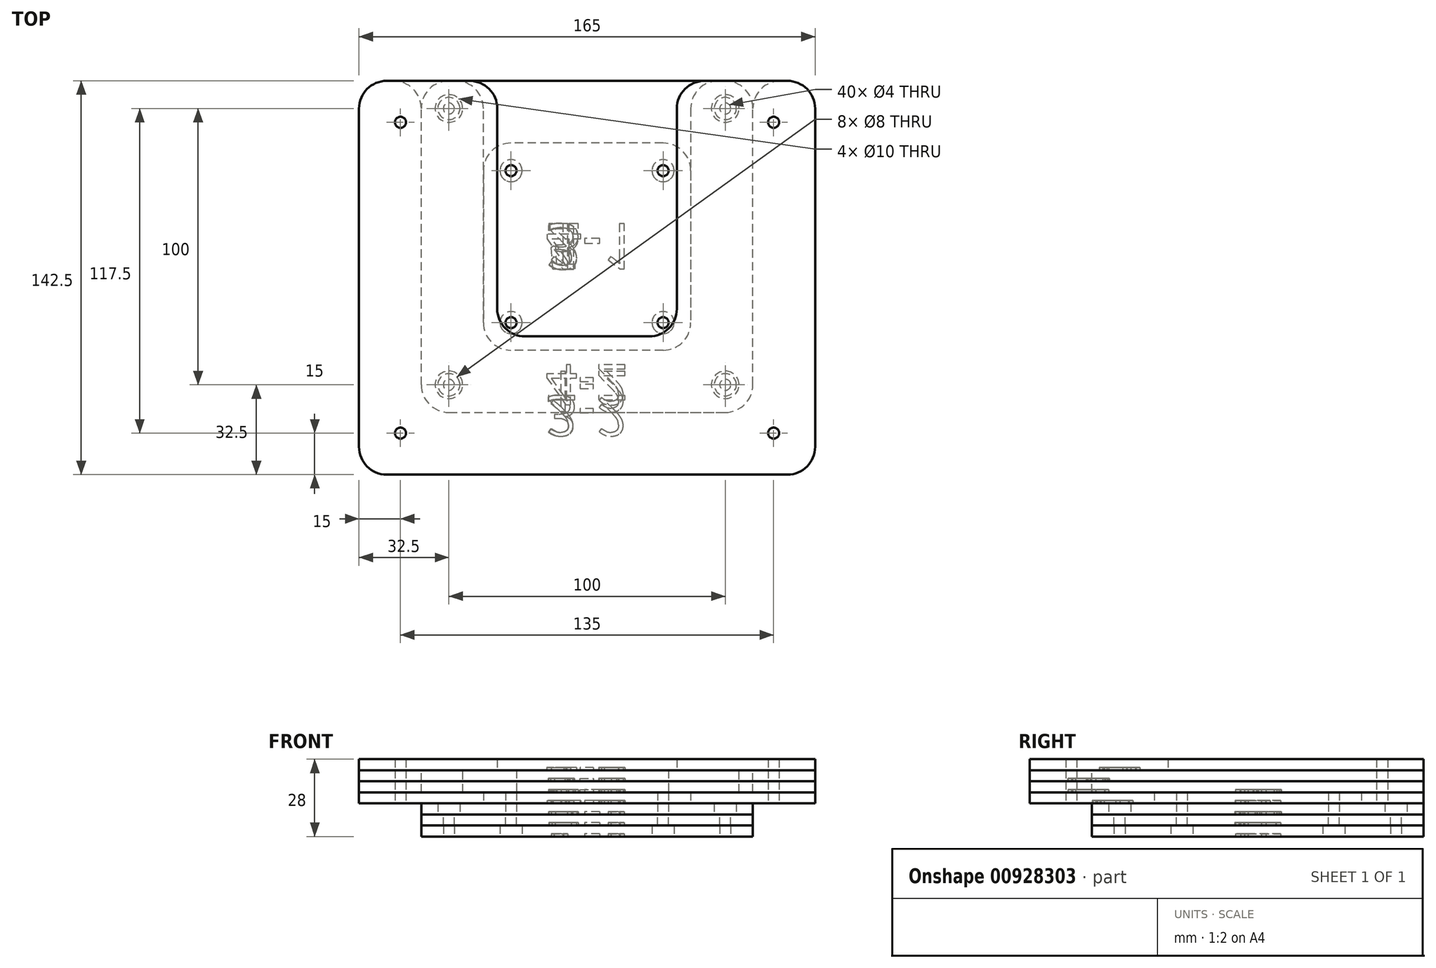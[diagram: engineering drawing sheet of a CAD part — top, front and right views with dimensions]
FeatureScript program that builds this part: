
annotation { "Feature Type Name" : "Feature", "Feature Type Description" : "" }
export const myFeature = defineFeature(function(context is Context, id is Id, definition is map)
    precondition{}
    {
        {
            var Q0;
            Q0=qCreatedBy(makeId("Top.planeOp"),FACE);
            var sketch = newSketch(context, id + "F0", { "sketchPlane" : qUnion([Q0])});
            skLineSegment(sketch, "E0.bottom", {"start": v(50, 50) * mm, "end": v(-50, 50) * mm, "construction": true});
            skLineSegment(sketch, "E0.top", {"start": v(50, -50) * mm, "end": v(-50, -50) * mm, "construction": true});
            skLineSegment(sketch, "E0.left", {"start": v(50, 50) * mm, "end": v(50, -50) * mm, "construction": true});
            skLineSegment(sketch, "E0.right", {"start": v(-50, 50) * mm, "end": v(-50, -50) * mm, "construction": true});
            skPoint(sketch, "E0.middle", {"position": v(0, 0) * mm});
            skCircle(sketch, "E1", {"center": v(-50, 50) * mm, "radius": 2 * mm});
            skCircle(sketch, "E2", {"center": v(50, 50) * mm, "radius": 2 * mm});
            skCircle(sketch, "E3", {"center": v(50, -50) * mm, "radius": 2 * mm});
            skCircle(sketch, "E4", {"center": v(-50, -50) * mm, "radius": 2 * mm});
            skLineSegment(sketch, "E5.bottom", {"start": v(60, 60) * mm, "end": v(-60, 60) * mm});
            skLineSegment(sketch, "E5.top", {"start": v(60, -60) * mm, "end": v(-60, -60) * mm});
            skLineSegment(sketch, "E5.left", {"start": v(60, 60) * mm, "end": v(60, -60) * mm});
            skLineSegment(sketch, "E5.right", {"start": v(-60, 60) * mm, "end": v(-60, -60) * mm});
            skSolve(sketch);
        }
        {
            var Q0;
            Q0 = qSketchRegion(id + "F0", true);
            extrude(context, id + "F1", {"entities" : qUnion([Q0]), "depth" : 4 * mm, "offsetDistance" : 25 * mm});
        }
        {
            var Q0;
            Q0=makeQuery(id+"F1.opExtrude","SWEPT_EDGE",EDGE,{"disambiguationData":[OSD([sQuery(id+"F0.wireOp",EDGE,"E5.bottom"),sQuery(id+"F0.wireOp",EDGE,"E5.right")])]});
            var Q1;
            Q1=makeQuery(id+"F1.opExtrude","SWEPT_EDGE",EDGE,{"disambiguationData":[OSD([sQuery(id+"F0.wireOp",EDGE,"E5.bottom"),sQuery(id+"F0.wireOp",EDGE,"E5.left")])]});
            var Q2;
            Q2=makeQuery(id+"F1.opExtrude","SWEPT_EDGE",EDGE,{"disambiguationData":[OSD([sQuery(id+"F0.wireOp",EDGE,"E5.top"),sQuery(id+"F0.wireOp",EDGE,"E5.right")])]});
            var Q3;
            Q3=makeQuery(id+"F1.opExtrude","SWEPT_EDGE",EDGE,{"disambiguationData":[OSD([sQuery(id+"F0.wireOp",EDGE,"E5.top"),sQuery(id+"F0.wireOp",EDGE,"E5.left")])]});
            fillet(context, id + "F2", {"entities" : qUnion([Q0, Q1, Q2, Q3]), "radius" : 10 * mm, "tangentPropagation" : true, "allowEdgeOverflow" : false});
        }
        {
            var Q0;
            Q0=makeQuery(id+"F1.opExtrude","CAP_FACE",FACE,{"disambiguationData":[OSD([sQuery(id+"F0.wireOp",EDGE,"E1"),sQuery(id+"F0.wireOp",EDGE,"E2"),sQuery(id+"F0.wireOp",EDGE,"E3"),sQuery(id+"F0.wireOp",EDGE,"E4"),sQuery(id+"F0.wireOp",EDGE,"E5.bottom"),sQuery(id+"F0.wireOp",EDGE,"E5.top"),sQuery(id+"F0.wireOp",EDGE,"E5.left"),sQuery(id+"F0.wireOp",EDGE,"E5.right")])],"isStart":false});
            var sketch = newSketch(context, id + "F3", { "sketchPlane" : qUnion([Q0])});
            skLineSegment(sketch, "E6.0.0", {"start": v(-50, -60) * mm, "end": v(50, -60) * mm});
            skArc(sketch, "E6.0.1", {"start": v(50, -60) * mm, "mid": v(57.07, -57.07) * mm, "end": v(60, -50) * mm});
            skLineSegment(sketch, "E6.0.2", {"start": v(60, -50) * mm, "end": v(60, 50) * mm});
            skArc(sketch, "E6.0.3", {"start": v(60, 50) * mm, "mid": v(57.07, 57.07) * mm, "end": v(50, 60) * mm});
            skLineSegment(sketch, "E6.0.4", {"start": v(50, 60) * mm, "end": v(-50, 60) * mm});
            skArc(sketch, "E6.0.5", {"start": v(-50, 60) * mm, "mid": v(-57.07, 57.07) * mm, "end": v(-60, 50) * mm});
            skLineSegment(sketch, "E6.0.6", {"start": v(-60, 50) * mm, "end": v(-60, -50) * mm});
            skArc(sketch, "E6.0.7", {"start": v(-60, -50) * mm, "mid": v(-57.07, -57.07) * mm, "end": v(-50, -60) * mm});
            skCircle(sketch, "E7.0", {"center": v(-50, 50) * mm, "radius": 2 * mm, "construction": true});
            skCircle(sketch, "E8.0", {"center": v(50, 50) * mm, "radius": 2 * mm, "construction": true});
            skCircle(sketch, "E9.0", {"center": v(50, -50) * mm, "radius": 2 * mm, "construction": true});
            skCircle(sketch, "E10.0", {"center": v(-50, -50) * mm, "radius": 2 * mm, "construction": true});
            skCircle(sketch, "E11", {"center": v(-50, 50) * mm, "radius": 4 * mm});
            skCircle(sketch, "E12", {"center": v(50, 50) * mm, "radius": 4 * mm});
            skCircle(sketch, "E13", {"center": v(50, -50) * mm, "radius": 4 * mm});
            skCircle(sketch, "E14", {"center": v(-50, -50) * mm, "radius": 4 * mm});
            skSolve(sketch);
        }
        {
            var Q0;
            Q0 = qSketchRegion(id + "F3", true);
            extrude(context, id + "F4", {"entities" : qUnion([Q0]), "depth" : 4 * mm, "offsetDistance" : 25 * mm});
        }
        {
            var Q0;
            Q0=makeQuery(id+"F4.opExtrude","CAP_FACE",FACE,{"disambiguationData":[OSD([sQuery(id+"F3.wireOp",EDGE,"E6.0.0"),sQuery(id+"F3.wireOp",EDGE,"E6.0.1"),sQuery(id+"F3.wireOp",EDGE,"E6.0.2"),sQuery(id+"F3.wireOp",EDGE,"E6.0.3"),sQuery(id+"F3.wireOp",EDGE,"E6.0.4"),sQuery(id+"F3.wireOp",EDGE,"E6.0.5"),sQuery(id+"F3.wireOp",EDGE,"E6.0.6"),sQuery(id+"F3.wireOp",EDGE,"E6.0.7"),sQuery(id+"F3.wireOp",EDGE,"E7.0"),sQuery(id+"F3.wireOp",EDGE,"E8.0"),sQuery(id+"F3.wireOp",EDGE,"E9.0"),sQuery(id+"F3.wireOp",EDGE,"E10.0")])],"isStart":false});
            var sketch = newSketch(context, id + "F5", { "sketchPlane" : qUnion([Q0])});
            skLineSegment(sketch, "E15.bottom", {"start": v(37.5, 37.5) * mm, "end": v(-37.5, 37.5) * mm});
            skLineSegment(sketch, "E15.top", {"start": v(37.5, -37.5) * mm, "end": v(-37.5, -37.5) * mm});
            skLineSegment(sketch, "E15.left", {"start": v(37.5, 37.5) * mm, "end": v(37.5, -37.5) * mm});
            skLineSegment(sketch, "E15.right", {"start": v(-37.5, 37.5) * mm, "end": v(-37.5, -37.5) * mm});
            skPoint(sketch, "E15.middle", {"position": v(0, 0) * mm});
            skSolve(sketch);
        }
        {
            var Q0;
            Q0 = qSketchRegion(id + "F5", true);
            extrude(context, id + "F6", {"entities" : qUnion([Q0]), "depth" : 4 * mm, "offsetDistance" : 25 * mm});
        }
        {
            var Q0;
            Q0=makeQuery(id+"F6.opExtrude","SWEPT_EDGE",EDGE,{"disambiguationData":[OSD([sQuery(id+"F5.wireOp",EDGE,"E15.bottom"),sQuery(id+"F5.wireOp",EDGE,"E15.right")])]});
            var Q1;
            Q1=makeQuery(id+"F6.opExtrude","SWEPT_EDGE",EDGE,{"disambiguationData":[OSD([sQuery(id+"F5.wireOp",EDGE,"E15.bottom"),sQuery(id+"F5.wireOp",EDGE,"E15.left")])]});
            var Q2;
            Q2=makeQuery(id+"F6.opExtrude","SWEPT_EDGE",EDGE,{"disambiguationData":[OSD([sQuery(id+"F5.wireOp",EDGE,"E15.top"),sQuery(id+"F5.wireOp",EDGE,"E15.left")])]});
            var Q3;
            Q3=makeQuery(id+"F6.opExtrude","SWEPT_EDGE",EDGE,{"disambiguationData":[OSD([sQuery(id+"F5.wireOp",EDGE,"E15.top"),sQuery(id+"F5.wireOp",EDGE,"E15.right")])]});
            fillet(context, id + "F7", {"entities" : qUnion([Q0, Q1, Q2, Q3]), "radius" : 10 * mm, "tangentPropagation" : true, "allowEdgeOverflow" : false});
        }
        {
            var Q0;
            Q0=makeQuery(id+"F6.opExtrude","CAP_FACE",FACE,{"disambiguationData":[OSD([sQuery(id+"F5.wireOp",EDGE,"E15.bottom"),sQuery(id+"F5.wireOp",EDGE,"E15.top"),sQuery(id+"F5.wireOp",EDGE,"E15.left"),sQuery(id+"F5.wireOp",EDGE,"E15.right")])],"isStart":false});
            var sketch = newSketch(context, id + "F8", { "sketchPlane" : qUnion([Q0])});
            skLineSegment(sketch, "E16.0.0", {"start": v(-50, -60) * mm, "end": v(50, -60) * mm});
            skArc(sketch, "E16.0.1", {"start": v(50, -60) * mm, "mid": v(57.07, -57.07) * mm, "end": v(60, -50) * mm});
            skLineSegment(sketch, "E16.0.2", {"start": v(60, -50) * mm, "end": v(60, 50) * mm});
            skArc(sketch, "E16.0.3", {"start": v(60, 50) * mm, "mid": v(57.07, 57.07) * mm, "end": v(50, 60) * mm});
            skLineSegment(sketch, "E16.0.4", {"start": v(50, 60) * mm, "end": v(-50, 60) * mm});
            skArc(sketch, "E16.0.5", {"start": v(-50, 60) * mm, "mid": v(-57.07, 57.07) * mm, "end": v(-60, 50) * mm});
            skLineSegment(sketch, "E16.0.6", {"start": v(-60, 50) * mm, "end": v(-60, -50) * mm});
            skArc(sketch, "E16.0.7", {"start": v(-60, -50) * mm, "mid": v(-57.07, -57.07) * mm, "end": v(-50, -60) * mm});
            skSolve(sketch);
        }
        {
            var Q0;
            Q0 = qSketchRegion(id + "F8", true);
            extrude(context, id + "F9", {"entities" : qUnion([Q0]), "depth" : 4 * mm, "offsetDistance" : 25 * mm});
        }
        {
            var Q0;
            Q0=makeQuery(id+"F1.opExtrude","CAP_FACE",FACE,{"disambiguationData":[OSD([sQuery(id+"F0.wireOp",EDGE,"E1"),sQuery(id+"F0.wireOp",EDGE,"E2"),sQuery(id+"F0.wireOp",EDGE,"E3"),sQuery(id+"F0.wireOp",EDGE,"E4"),sQuery(id+"F0.wireOp",EDGE,"E5.bottom"),sQuery(id+"F0.wireOp",EDGE,"E5.top"),sQuery(id+"F0.wireOp",EDGE,"E5.left"),sQuery(id+"F0.wireOp",EDGE,"E5.right")])],"isStart":true});
            var sketch = newSketch(context, id + "F10", { "sketchPlane" : qUnion([Q0])});
            skLineSegment(sketch, "E17.0.0", {"start": v(37.5, -27.5) * mm, "end": v(37.5, 27.5) * mm, "construction": true});
            skArc(sketch, "E17.0.1", {"start": v(37.5, 27.5) * mm, "mid": v(34.57, 34.57) * mm, "end": v(27.5, 37.5) * mm, "construction": true});
            skLineSegment(sketch, "E17.0.2", {"start": v(27.5, 37.5) * mm, "end": v(-27.5, 37.5) * mm, "construction": true});
            skArc(sketch, "E17.0.3", {"start": v(-27.5, 37.5) * mm, "mid": v(-34.57, 34.57) * mm, "end": v(-37.5, 27.5) * mm, "construction": true});
            skLineSegment(sketch, "E17.0.4", {"start": v(-37.5, 27.5) * mm, "end": v(-37.5, -27.5) * mm, "construction": true});
            skArc(sketch, "E17.0.5", {"start": v(-37.5, -27.5) * mm, "mid": v(-34.57, -34.57) * mm, "end": v(-27.5, -37.5) * mm, "construction": true});
            skLineSegment(sketch, "E17.0.6", {"start": v(-27.5, -37.5) * mm, "end": v(27.5, -37.5) * mm, "construction": true});
            skArc(sketch, "E17.0.7", {"start": v(27.5, -37.5) * mm, "mid": v(34.57, -34.57) * mm, "end": v(37.5, -27.5) * mm, "construction": true});
            skCircle(sketch, "E18", {"center": v(27.5, -27.5) * mm, "radius": 4 * mm});
            skCircle(sketch, "E19", {"center": v(-27.5, -27.5) * mm, "radius": 4 * mm});
            skCircle(sketch, "E20", {"center": v(27.5, 27.5) * mm, "radius": 4 * mm});
            skCircle(sketch, "E21", {"center": v(-27.5, 27.5) * mm, "radius": 4 * mm});
            skCircle(sketch, "E22", {"center": v(27.5, -27.5) * mm, "radius": 2 * mm});
            skCircle(sketch, "E23", {"center": v(-27.5, -27.5) * mm, "radius": 2 * mm});
            skCircle(sketch, "E24", {"center": v(-27.5, 27.5) * mm, "radius": 2 * mm});
            skCircle(sketch, "E25", {"center": v(27.5, 27.5) * mm, "radius": 2 * mm});
            skSolve(sketch);
        }
        {
            var Q0;
            Q0=makeQuery(id+"F10.imprint","IMPRINT",FACE,{"disambiguationData":[TD([[makeQuery(id+"F10.imprint","IMPRINT",EDGE,{"derivedFrom":sQuery(id+"F10.wireOp",EDGE,"E22")}),1.0]])]});
            var Q1;
            Q1=makeQuery(id+"F10.imprint","IMPRINT",FACE,{"disambiguationData":[TD([[makeQuery(id+"F10.imprint","IMPRINT",EDGE,{"derivedFrom":sQuery(id+"F10.wireOp",EDGE,"E18")}),1.0]])]});
            var Q2;
            Q2=makeQuery(id+"F10.imprint","IMPRINT",FACE,{"disambiguationData":[TD([[makeQuery(id+"F10.imprint","IMPRINT",EDGE,{"derivedFrom":sQuery(id+"F10.wireOp",EDGE,"E19")}),1.0]])]});
            var Q3;
            Q3=makeQuery(id+"F10.imprint","IMPRINT",FACE,{"disambiguationData":[TD([[makeQuery(id+"F10.imprint","IMPRINT",EDGE,{"derivedFrom":sQuery(id+"F10.wireOp",EDGE,"E23")}),1.0]])]});
            var Q4;
            Q4=makeQuery(id+"F10.imprint","IMPRINT",FACE,{"disambiguationData":[TD([[makeQuery(id+"F10.imprint","IMPRINT",EDGE,{"derivedFrom":sQuery(id+"F10.wireOp",EDGE,"E24")}),1.0]])]});
            var Q5;
            Q5=makeQuery(id+"F10.imprint","IMPRINT",FACE,{"disambiguationData":[TD([[makeQuery(id+"F10.imprint","IMPRINT",EDGE,{"derivedFrom":sQuery(id+"F10.wireOp",EDGE,"E21")}),1.0]])]});
            var Q6;
            Q6=makeQuery(id+"F10.imprint","IMPRINT",FACE,{"disambiguationData":[TD([[makeQuery(id+"F10.imprint","IMPRINT",EDGE,{"derivedFrom":sQuery(id+"F10.wireOp",EDGE,"E20")}),1.0]])]});
            var Q7;
            Q7=makeQuery(id+"F10.imprint","IMPRINT",FACE,{"disambiguationData":[TD([[makeQuery(id+"F10.imprint","IMPRINT",EDGE,{"derivedFrom":sQuery(id+"F10.wireOp",EDGE,"E25")}),1.0]])]});
            var Q8;
            Q8=makeQuery(id+"F1.opExtrude","CAP_FACE",FACE,{"disambiguationData":[OSD([sQuery(id+"F0.wireOp",EDGE,"E1"),sQuery(id+"F0.wireOp",EDGE,"E2"),sQuery(id+"F0.wireOp",EDGE,"E3"),sQuery(id+"F0.wireOp",EDGE,"E4"),sQuery(id+"F0.wireOp",EDGE,"E5.bottom"),sQuery(id+"F0.wireOp",EDGE,"E5.top"),sQuery(id+"F0.wireOp",EDGE,"E5.left"),sQuery(id+"F0.wireOp",EDGE,"E5.right")])],"isStart":false});
            extrude(context, id + "F11", {"entities" : qUnion([Q0, Q1, Q2, Q3, Q4, Q5, Q6, Q7]), "operationType" : NewBodyOperationType.REMOVE, "endBound" : BoundingType.UP_TO_SURFACE, "oppositeDirection" : true, "depth" : 25 * mm, "endBoundEntityFace" : qUnion([Q8]), "offsetDistance" : 25 * mm});
        }
        {
            var Q0;
            Q0=makeQuery(id+"F10.imprint","IMPRINT",FACE,{"disambiguationData":[TD([[makeQuery(id+"F10.imprint","IMPRINT",EDGE,{"derivedFrom":sQuery(id+"F10.wireOp",EDGE,"E22")}),1.0]])]});
            var Q1;
            Q1=makeQuery(id+"F10.imprint","IMPRINT",FACE,{"disambiguationData":[TD([[makeQuery(id+"F10.imprint","IMPRINT",EDGE,{"derivedFrom":sQuery(id+"F10.wireOp",EDGE,"E23")}),1.0]])]});
            var Q2;
            Q2=makeQuery(id+"F10.imprint","IMPRINT",FACE,{"disambiguationData":[TD([[makeQuery(id+"F10.imprint","IMPRINT",EDGE,{"derivedFrom":sQuery(id+"F10.wireOp",EDGE,"E24")}),1.0]])]});
            var Q3;
            Q3=makeQuery(id+"F10.imprint","IMPRINT",FACE,{"disambiguationData":[TD([[makeQuery(id+"F10.imprint","IMPRINT",EDGE,{"derivedFrom":sQuery(id+"F10.wireOp",EDGE,"E25")}),1.0]])]});
            extrude(context, id + "F12", {"entities" : qUnion([Q0, Q1, Q2, Q3]), "operationType" : NewBodyOperationType.REMOVE, "endBound" : BoundingType.THROUGH_ALL, "oppositeDirection" : true, "depth" : 25 * mm, "offsetDistance" : 25 * mm});
        }
        {
            var Q0;
            Q0=makeQuery(id+"F9.opExtrude","CAP_FACE",FACE,{"disambiguationData":[OSD([sQuery(id+"F8.wireOp",EDGE,"E16.0.0"),sQuery(id+"F8.wireOp",EDGE,"E16.0.1"),sQuery(id+"F8.wireOp",EDGE,"E16.0.2"),sQuery(id+"F8.wireOp",EDGE,"E16.0.3"),sQuery(id+"F8.wireOp",EDGE,"E16.0.4"),sQuery(id+"F8.wireOp",EDGE,"E16.0.5"),sQuery(id+"F8.wireOp",EDGE,"E16.0.6"),sQuery(id+"F8.wireOp",EDGE,"E16.0.7")])],"isStart":false});
            var sketch = newSketch(context, id + "F13", { "sketchPlane" : qUnion([Q0])});
            skCircle(sketch, "E26.0", {"center": v(-27.5, 27.5) * mm, "radius": 2 * mm});
            skCircle(sketch, "E27.0", {"center": v(27.5, 27.5) * mm, "radius": 2 * mm});
            skCircle(sketch, "E28.0", {"center": v(27.5, -27.5) * mm, "radius": 2 * mm});
            skCircle(sketch, "E29.0", {"center": v(-27.5, -27.5) * mm, "radius": 2 * mm});
            skLineSegment(sketch, "E30.0.0", {"start": v(-60, 50) * mm, "end": v(-60, -50) * mm});
            skArc(sketch, "E30.0.1", {"start": v(-60, -50) * mm, "mid": v(-57.07, -57.07) * mm, "end": v(-50, -60) * mm});
            skLineSegment(sketch, "E30.0.2", {"start": v(-50, -60) * mm, "end": v(50, -60) * mm});
            skArc(sketch, "E30.0.3", {"start": v(50, -60) * mm, "mid": v(57.07, -57.07) * mm, "end": v(60, -50) * mm});
            skLineSegment(sketch, "E30.0.4", {"start": v(60, -50) * mm, "end": v(60, 50) * mm});
            skArc(sketch, "E30.0.5", {"start": v(60, 50) * mm, "mid": v(57.07, 57.07) * mm, "end": v(50, 60) * mm});
            skLineSegment(sketch, "E30.0.6", {"start": v(50, 60) * mm, "end": v(-50, 60) * mm});
            skArc(sketch, "E30.0.7", {"start": v(-50, 60) * mm, "mid": v(-57.07, 57.07) * mm, "end": v(-60, 50) * mm});
            skSolve(sketch);
        }
        {
            var Q0;
            Q0 = qSketchRegion(id + "F13", true);
            extrude(context, id + "F14", {"entities" : qUnion([Q0]), "depth" : 4 * mm, "offsetDistance" : 25 * mm});
        }
        {
            var Q0;
            Q0=makeQuery(id+"F14.opExtrude","CAP_FACE",FACE,{"disambiguationData":[OSD([sQuery(id+"F13.wireOp",EDGE,"E26.0"),sQuery(id+"F13.wireOp",EDGE,"E27.0"),sQuery(id+"F13.wireOp",EDGE,"E28.0"),sQuery(id+"F13.wireOp",EDGE,"E29.0"),sQuery(id+"F13.wireOp",EDGE,"E30.0.0"),sQuery(id+"F13.wireOp",EDGE,"E30.0.1"),sQuery(id+"F13.wireOp",EDGE,"E30.0.2"),sQuery(id+"F13.wireOp",EDGE,"E30.0.3"),sQuery(id+"F13.wireOp",EDGE,"E30.0.4"),sQuery(id+"F13.wireOp",EDGE,"E30.0.5"),sQuery(id+"F13.wireOp",EDGE,"E30.0.6"),sQuery(id+"F13.wireOp",EDGE,"E30.0.7")])],"isStart":false});
            var sketch = newSketch(context, id + "F15", { "sketchPlane" : qUnion([Q0])});
            skLineSegment(sketch, "E31", {"start": v(0, -32.5) * mm, "end": v(32.5, -32.5) * mm});
            skLineSegment(sketch, "E32", {"start": v(32.5, -32.5) * mm, "end": v(32.5, 60) * mm});
            skLineSegment(sketch, "E33", {"start": v(32.5, 60) * mm, "end": v(82.5, 60) * mm});
            skLineSegment(sketch, "E34", {"start": v(82.5, 60) * mm, "end": v(82.5, -82.5) * mm});
            skLineSegment(sketch, "E35", {"start": v(82.5, -82.5) * mm, "end": v(0, -82.5) * mm});
            skLineSegment(sketch, "E36", {"start": v(0, -32.5) * mm, "end": v(0, -82.5) * mm, "construction": true});
            skLineSegment(sketch, "E37.bottom", {"start": v(27.5, -27.5) * mm, "end": v(32.5, -27.5) * mm, "construction": true});
            skLineSegment(sketch, "E37.top", {"start": v(27.5, -32.5) * mm, "end": v(32.5, -32.5) * mm, "construction": true});
            skLineSegment(sketch, "E37.left", {"start": v(27.5, -27.5) * mm, "end": v(27.5, -32.5) * mm, "construction": true});
            skLineSegment(sketch, "E37.right", {"start": v(32.5, -27.5) * mm, "end": v(32.5, -32.5) * mm, "construction": true});
            skLineSegment(sketch, "E38.MirrorCS", {"start": v(0, -32.5) * mm, "end": v(-32.5, -32.5) * mm});
            skLineSegment(sketch, "E39.MirrorCS", {"start": v(-32.5, -32.5) * mm, "end": v(-32.5, 60) * mm});
            skLineSegment(sketch, "E40.MirrorCS", {"start": v(-32.5, 60) * mm, "end": v(-82.5, 60) * mm});
            skLineSegment(sketch, "E41.MirrorCS", {"start": v(-82.5, 60) * mm, "end": v(-82.5, -82.5) * mm});
            skLineSegment(sketch, "E42.MirrorCS", {"start": v(-82.5, -82.5) * mm, "end": v(0, -82.5) * mm});
            skSolve(sketch);
        }
        {
            var Q0;
            Q0 = qSketchRegion(id + "F15", true);
            extrude(context, id + "F16", {"entities" : qUnion([Q0]), "depth" : 4 * mm, "offsetDistance" : 25 * mm});
        }
        {
            var Q0;
            Q0=makeQuery(id+"F16.opExtrude","SWEPT_EDGE",EDGE,{"disambiguationData":[OSD([sQuery(id+"F13.wireOp",EDGE,"E30.0.6"),sQuery(id+"F15.wireOp",EDGE,"E39.MirrorCS"),sQuery(id+"F15.wireOp",EDGE,"E40.MirrorCS")])]});
            var Q1;
            Q1=makeQuery(id+"F16.opExtrude","SWEPT_EDGE",EDGE,{"disambiguationData":[OSD([sQuery(id+"F15.wireOp",EDGE,"E33"),sQuery(id+"F15.wireOp",EDGE,"E34")])]});
            var Q2;
            Q2=makeQuery(id+"F16.opExtrude","SWEPT_EDGE",EDGE,{"disambiguationData":[OSD([sQuery(id+"F15.wireOp",EDGE,"E34"),sQuery(id+"F15.wireOp",EDGE,"E35")])]});
            var Q3;
            Q3=makeQuery(id+"F16.opExtrude","SWEPT_EDGE",EDGE,{"disambiguationData":[OSD([sQuery(id+"F15.wireOp",EDGE,"E38.MirrorCS"),sQuery(id+"F15.wireOp",EDGE,"E39.MirrorCS")])]});
            var Q4;
            Q4=makeQuery(id+"F16.opExtrude","SWEPT_EDGE",EDGE,{"disambiguationData":[OSD([sQuery(id+"F15.wireOp",EDGE,"E40.MirrorCS"),sQuery(id+"F15.wireOp",EDGE,"E41.MirrorCS")])]});
            var Q5;
            Q5=makeQuery(id+"F16.opExtrude","SWEPT_EDGE",EDGE,{"disambiguationData":[OSD([sQuery(id+"F13.wireOp",EDGE,"E30.0.6"),sQuery(id+"F15.wireOp",EDGE,"E32"),sQuery(id+"F15.wireOp",EDGE,"E33")])]});
            var Q6;
            Q6=makeQuery(id+"F16.opExtrude","SWEPT_EDGE",EDGE,{"disambiguationData":[OSD([sQuery(id+"F15.wireOp",EDGE,"E31"),sQuery(id+"F15.wireOp",EDGE,"E32")])]});
            var Q7;
            Q7=makeQuery(id+"F16.opExtrude","SWEPT_EDGE",EDGE,{"disambiguationData":[OSD([sQuery(id+"F15.wireOp",EDGE,"E41.MirrorCS"),sQuery(id+"F15.wireOp",EDGE,"E42.MirrorCS")])]});
            fillet(context, id + "F17", {"entities" : qUnion([Q0, Q1, Q2, Q3, Q4, Q5, Q6, Q7]), "radius" : 10 * mm, "tangentPropagation" : true, "allowEdgeOverflow" : false});
        }
        {
            var Q0;
            Q0=makeQuery(id+"F16.opExtrude","CAP_FACE",FACE,{"disambiguationData":[OSD([sQuery(id+"F15.wireOp",EDGE,"E31"),sQuery(id+"F15.wireOp",EDGE,"E32"),sQuery(id+"F15.wireOp",EDGE,"E33"),sQuery(id+"F15.wireOp",EDGE,"E34"),sQuery(id+"F15.wireOp",EDGE,"E35"),sQuery(id+"F15.wireOp",EDGE,"E38.MirrorCS"),sQuery(id+"F15.wireOp",EDGE,"E39.MirrorCS"),sQuery(id+"F15.wireOp",EDGE,"E40.MirrorCS"),sQuery(id+"F15.wireOp",EDGE,"E41.MirrorCS"),sQuery(id+"F15.wireOp",EDGE,"E42.MirrorCS")])],"isStart":true});
            var sketch = newSketch(context, id + "F18", { "sketchPlane" : qUnion([Q0])});
            skLineSegment(sketch, "E43.0", {"start": v(60, 50) * mm, "end": v(60, -50) * mm});
            skArc(sketch, "E44.0", {"start": v(50, 60) * mm, "mid": v(57.07, 57.07) * mm, "end": v(60, 50) * mm});
            skLineSegment(sketch, "E45.0", {"start": v(-50, 60) * mm, "end": v(50, 60) * mm});
            skArc(sketch, "E46.0", {"start": v(-60, 50) * mm, "mid": v(-57.07, 57.07) * mm, "end": v(-50, 60) * mm});
            skLineSegment(sketch, "E47.0", {"start": v(-60, -50) * mm, "end": v(-60, 50) * mm});
            skLineSegment(sketch, "E48.0", {"start": v(-82.5, -50) * mm, "end": v(-82.5, 72.5) * mm});
            skArc(sketch, "E49.0", {"start": v(-72.5, 82.5) * mm, "mid": v(-79.57, 79.57) * mm, "end": v(-82.5, 72.5) * mm});
            skLineSegment(sketch, "E50.0", {"start": v(-72.5, 82.5) * mm, "end": v(72.5, 82.5) * mm});
            skArc(sketch, "E51.0", {"start": v(82.5, 72.5) * mm, "mid": v(79.57, 79.57) * mm, "end": v(72.5, 82.5) * mm});
            skLineSegment(sketch, "E52.0", {"start": v(82.5, -50) * mm, "end": v(82.5, 72.5) * mm});
            skArc(sketch, "E53.0", {"start": v(72.5, -60) * mm, "mid": v(79.57, -57.07) * mm, "end": v(82.5, -50) * mm});
            skArc(sketch, "E54.0", {"start": v(-82.5, -50) * mm, "mid": v(-79.57, -57.07) * mm, "end": v(-72.5, -60) * mm});
            skLineSegment(sketch, "E55", {"start": v(-60, -50) * mm, "end": v(-60, -60) * mm});
            skPoint(sketch, "E55.endSnap0", {"position": v(-57.5, -60) * mm});
            skLineSegment(sketch, "E56", {"start": v(-60, -60) * mm, "end": v(-72.5, -60) * mm});
            skLineSegment(sketch, "E57", {"start": v(60, -50) * mm, "end": v(60, -60) * mm});
            skLineSegment(sketch, "E58", {"start": v(60, -60) * mm, "end": v(72.5, -60) * mm});
            skSolve(sketch);
        }
        {
            var Q0;
            Q0 = qSketchRegion(id + "F18", true);
            extrude(context, id + "F19", {"entities" : qUnion([Q0]), "depth" : 4 * mm, "offsetDistance" : 25 * mm});
        }
        {
            var Q0;
            Q0=makeQuery(id+"F19.opExtrude","SWEPT_EDGE",EDGE,{"disambiguationData":[OSD([sQuery(id+"F15.wireOp",EDGE,"E40.MirrorCS"),sQuery(id+"F18.wireOp",EDGE,"E55"),sQuery(id+"F18.wireOp",EDGE,"E56")])]});
            var Q1;
            Q1=makeQuery(id+"F19.opExtrude","SWEPT_EDGE",EDGE,{"disambiguationData":[OSD([sQuery(id+"F15.wireOp",EDGE,"E33"),sQuery(id+"F18.wireOp",EDGE,"E57"),sQuery(id+"F18.wireOp",EDGE,"E58")])]});
            fillet(context, id + "F20", {"entities" : qUnion([Q0, Q1]), "radius" : 10 * mm, "tangentPropagation" : true, "allowEdgeOverflow" : false});
        }
        {
            var Q0;
            Q0=makeQuery(id+"F19.opExtrude","CAP_FACE",FACE,{"disambiguationData":[OSD([sQuery(id+"F18.wireOp",EDGE,"E43.0"),sQuery(id+"F18.wireOp",EDGE,"E44.0"),sQuery(id+"F18.wireOp",EDGE,"E45.0"),sQuery(id+"F18.wireOp",EDGE,"E46.0"),sQuery(id+"F18.wireOp",EDGE,"E47.0"),sQuery(id+"F18.wireOp",EDGE,"E48.0"),sQuery(id+"F18.wireOp",EDGE,"E49.0"),sQuery(id+"F18.wireOp",EDGE,"E50.0"),sQuery(id+"F18.wireOp",EDGE,"E51.0"),sQuery(id+"F18.wireOp",EDGE,"E52.0"),sQuery(id+"F18.wireOp",EDGE,"E53.0"),sQuery(id+"F18.wireOp",EDGE,"E54.0"),sQuery(id+"F18.wireOp",EDGE,"E55"),sQuery(id+"F18.wireOp",EDGE,"E56"),sQuery(id+"F18.wireOp",EDGE,"E57"),sQuery(id+"F18.wireOp",EDGE,"E58")])],"isStart":false});
            var sketch = newSketch(context, id + "F21", { "sketchPlane" : qUnion([Q0])});
            skLineSegment(sketch, "E59.0.0", {"start": v(60, 50) * mm, "end": v(60, -50) * mm});
            skArc(sketch, "E59.0.1", {"start": v(60, -50) * mm, "mid": v(62.93, -57.07) * mm, "end": v(70, -60) * mm});
            skLineSegment(sketch, "E59.0.2", {"start": v(70, -60) * mm, "end": v(72.5, -60) * mm});
            skArc(sketch, "E59.0.3", {"start": v(72.5, -60) * mm, "mid": v(79.57, -57.07) * mm, "end": v(82.5, -50) * mm});
            skLineSegment(sketch, "E59.0.4", {"start": v(82.5, -50) * mm, "end": v(82.5, 72.5) * mm});
            skArc(sketch, "E59.0.5", {"start": v(82.5, 72.5) * mm, "mid": v(79.57, 79.57) * mm, "end": v(72.5, 82.5) * mm});
            skLineSegment(sketch, "E59.0.6", {"start": v(72.5, 82.5) * mm, "end": v(-72.5, 82.5) * mm});
            skArc(sketch, "E59.0.7", {"start": v(-72.5, 82.5) * mm, "mid": v(-79.57, 79.57) * mm, "end": v(-82.5, 72.5) * mm});
            skLineSegment(sketch, "E59.0.8", {"start": v(-82.5, 72.5) * mm, "end": v(-82.5, -50) * mm});
            skArc(sketch, "E59.0.9", {"start": v(-82.5, -50) * mm, "mid": v(-79.57, -57.07) * mm, "end": v(-72.5, -60) * mm});
            skLineSegment(sketch, "E59.0.10", {"start": v(-72.5, -60) * mm, "end": v(-70, -60) * mm});
            skArc(sketch, "E59.0.11", {"start": v(-70, -60) * mm, "mid": v(-62.93, -57.07) * mm, "end": v(-60, -50) * mm});
            skLineSegment(sketch, "E59.0.12", {"start": v(-60, -50) * mm, "end": v(-60, 50) * mm});
            skArc(sketch, "E59.0.13", {"start": v(-60, 50) * mm, "mid": v(-57.07, 57.07) * mm, "end": v(-50, 60) * mm});
            skLineSegment(sketch, "E59.0.14", {"start": v(-50, 60) * mm, "end": v(50, 60) * mm});
            skArc(sketch, "E59.0.15", {"start": v(50, 60) * mm, "mid": v(57.07, 57.07) * mm, "end": v(60, 50) * mm});
            skSolve(sketch);
        }
        {
            var Q0;
            Q0 = qSketchRegion(id + "F21", true);
            extrude(context, id + "F22", {"entities" : qUnion([Q0]), "depth" : 4 * mm, "offsetDistance" : 25 * mm});
        }
        {
            var Q0;
            Q0=makeQuery(id+"F22.opExtrude","CAP_FACE",FACE,{"disambiguationData":[OSD([sQuery(id+"F21.wireOp",EDGE,"E59.0.0"),sQuery(id+"F21.wireOp",EDGE,"E59.0.1"),sQuery(id+"F21.wireOp",EDGE,"E59.0.2"),sQuery(id+"F21.wireOp",EDGE,"E59.0.3"),sQuery(id+"F21.wireOp",EDGE,"E59.0.4"),sQuery(id+"F21.wireOp",EDGE,"E59.0.5"),sQuery(id+"F21.wireOp",EDGE,"E59.0.6"),sQuery(id+"F21.wireOp",EDGE,"E59.0.7"),sQuery(id+"F21.wireOp",EDGE,"E59.0.8"),sQuery(id+"F21.wireOp",EDGE,"E59.0.9"),sQuery(id+"F21.wireOp",EDGE,"E59.0.10"),sQuery(id+"F21.wireOp",EDGE,"E59.0.11"),sQuery(id+"F21.wireOp",EDGE,"E59.0.12"),sQuery(id+"F21.wireOp",EDGE,"E59.0.13"),sQuery(id+"F21.wireOp",EDGE,"E59.0.14"),sQuery(id+"F21.wireOp",EDGE,"E59.0.15")])],"isStart":false});
            var sketch = newSketch(context, id + "F23", { "sketchPlane" : qUnion([Q0])});
            skLineSegment(sketch, "E60.0.3", {"start": v(70, -60) * mm, "end": v(72.5, -60) * mm});
            skArc(sketch, "E60.0.4", {"start": v(72.5, -60) * mm, "mid": v(79.57, -57.07) * mm, "end": v(82.5, -50) * mm});
            skLineSegment(sketch, "E60.0.5", {"start": v(82.5, -50) * mm, "end": v(82.5, 72.5) * mm});
            skArc(sketch, "E60.0.6", {"start": v(82.5, 72.5) * mm, "mid": v(79.57, 79.57) * mm, "end": v(72.5, 82.5) * mm});
            skLineSegment(sketch, "E60.0.7", {"start": v(72.5, 82.5) * mm, "end": v(-72.5, 82.5) * mm});
            skArc(sketch, "E60.0.8", {"start": v(-72.5, 82.5) * mm, "mid": v(-79.57, 79.57) * mm, "end": v(-82.5, 72.5) * mm});
            skLineSegment(sketch, "E60.0.9", {"start": v(-82.5, 72.5) * mm, "end": v(-82.5, -50) * mm});
            skArc(sketch, "E60.0.10", {"start": v(-82.5, -50) * mm, "mid": v(-79.57, -57.07) * mm, "end": v(-72.5, -60) * mm});
            skLineSegment(sketch, "E60.0.11", {"start": v(-72.5, -60) * mm, "end": v(-70, -60) * mm});
            skLineSegment(sketch, "E61.0.0", {"start": v(37.5, -27.5) * mm, "end": v(37.5, 27.5) * mm});
            skArc(sketch, "E61.0.1", {"start": v(37.5, 27.5) * mm, "mid": v(34.57, 34.57) * mm, "end": v(27.5, 37.5) * mm});
            skLineSegment(sketch, "E61.0.2", {"start": v(27.5, 37.5) * mm, "end": v(-27.5, 37.5) * mm});
            skArc(sketch, "E61.0.3", {"start": v(-27.5, 37.5) * mm, "mid": v(-34.57, 34.57) * mm, "end": v(-37.5, 27.5) * mm});
            skLineSegment(sketch, "E61.0.4", {"start": v(-37.5, 27.5) * mm, "end": v(-37.5, -27.5) * mm});
            skLineSegment(sketch, "E62", {"start": v(-37.5, -27.5) * mm, "end": v(-37.5, -50) * mm});
            skLineSegment(sketch, "E63", {"start": v(-47.5, -60) * mm, "end": v(-70, -60) * mm});
            skLineSegment(sketch, "E64", {"start": v(37.5, -27.5) * mm, "end": v(37.5, -50) * mm});
            skLineSegment(sketch, "E65", {"start": v(47.5, -60) * mm, "end": v(70, -60) * mm});
            skPoint(sketch, "E60.0.13.start.orphan", {"position": v(-60, -50) * mm});
            skPoint(sketch, "E60.0.14.start.orphan", {"position": v(-60, 50) * mm});
            skPoint(sketch, "E60.0.15.start.orphan", {"position": v(-50, 60) * mm});
            skPoint(sketch, "E60.0.0.start.orphan", {"position": v(50, 60) * mm});
            skPoint(sketch, "E60.0.1.start.orphan", {"position": v(60, 50) * mm});
            skPoint(sketch, "E60.0.2.start.orphan", {"position": v(60, -50) * mm});
            skPoint(sketch, "E61.0.6.end.orphan", {"position": v(27.5, -37.5) * mm});
            skPoint(sketch, "E61.0.5.end.orphan", {"position": v(-27.5, -37.5) * mm});
            skPoint(sketch, "E66.visualSharp", {"position": v(-37.5, -60) * mm});
            skArc(sketch, "E66.filletArc", {"start": v(-47.5, -60) * mm, "mid": v(-40.43, -57.07) * mm, "end": v(-37.5, -50) * mm});
            skPoint(sketch, "E67.visualSharp", {"position": v(37.5, -60) * mm});
            skArc(sketch, "E67.filletArc", {"start": v(37.5, -50) * mm, "mid": v(40.43, -57.07) * mm, "end": v(47.5, -60) * mm});
            skSolve(sketch);
        }
        {
            var Q0;
            Q0 = qSketchRegion(id + "F23", true);
            extrude(context, id + "F24", {"entities" : qUnion([Q0]), "depth" : 4 * mm, "offsetDistance" : 25 * mm});
        }
        {
            var Q0;
            Q0=makeQuery(id+"F24.opExtrude","CAP_FACE",FACE,{"disambiguationData":[OSD([sQuery(id+"F23.wireOp",EDGE,"E60.0.3"),sQuery(id+"F23.wireOp",EDGE,"E60.0.4"),sQuery(id+"F23.wireOp",EDGE,"E60.0.5"),sQuery(id+"F23.wireOp",EDGE,"E60.0.6"),sQuery(id+"F23.wireOp",EDGE,"E60.0.7"),sQuery(id+"F23.wireOp",EDGE,"E60.0.8"),sQuery(id+"F23.wireOp",EDGE,"E60.0.9"),sQuery(id+"F23.wireOp",EDGE,"E60.0.10"),sQuery(id+"F23.wireOp",EDGE,"E60.0.11"),sQuery(id+"F23.wireOp",EDGE,"E61.0.0"),sQuery(id+"F23.wireOp",EDGE,"E61.0.1"),sQuery(id+"F23.wireOp",EDGE,"E61.0.2"),sQuery(id+"F23.wireOp",EDGE,"E61.0.3"),sQuery(id+"F23.wireOp",EDGE,"E61.0.4"),sQuery(id+"F23.wireOp",EDGE,"E62"),sQuery(id+"F23.wireOp",EDGE,"E63"),sQuery(id+"F23.wireOp",EDGE,"E64"),sQuery(id+"F23.wireOp",EDGE,"E65"),sQuery(id+"F23.wireOp",EDGE,"E66.filletArc"),sQuery(id+"F23.wireOp",EDGE,"E67.filletArc")])],"isStart":false});
            var sketch = newSketch(context, id + "F25", { "sketchPlane" : qUnion([Q0])});
            skLineSegment(sketch, "E68.bottom", {"start": v(67.5, 67.5) * mm, "end": v(-67.5, 67.5) * mm, "construction": true});
            skLineSegment(sketch, "E68.top", {"start": v(67.5, -45) * mm, "end": v(-67.5, -45) * mm, "construction": true});
            skLineSegment(sketch, "E68.left", {"start": v(67.5, 67.5) * mm, "end": v(67.5, -45) * mm, "construction": true});
            skLineSegment(sketch, "E68.right", {"start": v(-67.5, 67.5) * mm, "end": v(-67.5, -45) * mm, "construction": true});
            skPoint(sketch, "E68.middle", {"position": v(0, 11.25) * mm});
            skCircle(sketch, "E69", {"center": v(-67.5, 67.5) * mm, "radius": 2 * mm});
            skCircle(sketch, "E70", {"center": v(67.5, 67.5) * mm, "radius": 2 * mm});
            skCircle(sketch, "E71", {"center": v(67.5, -45) * mm, "radius": 2 * mm});
            skCircle(sketch, "E72", {"center": v(-67.5, -45) * mm, "radius": 2 * mm});
            skLineSegment(sketch, "E73", {"start": v(-67.5, 67.5) * mm, "end": v(-82.5, 67.5) * mm, "construction": true});
            skLineSegment(sketch, "E74", {"start": v(-67.5, 67.5) * mm, "end": v(-67.5, 82.5) * mm, "construction": true});
            skLineSegment(sketch, "E75", {"start": v(-67.5, -45) * mm, "end": v(-67.5, -60) * mm, "construction": true});
            skLineSegment(sketch, "E76", {"start": v(-67.5, -45) * mm, "end": v(-82.5, -45) * mm, "construction": true});
            skSolve(sketch);
        }
        {
            var Q0;
            Q0 = qSketchRegion(id + "F25", true);
            extrude(context, id + "F26", {"entities" : qUnion([Q0]), "operationType" : NewBodyOperationType.REMOVE, "endBound" : BoundingType.THROUGH_ALL, "oppositeDirection" : true, "depth" : 25 * mm, "offsetDistance" : 25 * mm});
        }
        {
            var Q0;
            Q0=makeQuery(id+"F14.opExtrude","CAP_FACE",FACE,{"disambiguationData":[OSD([sQuery(id+"F13.wireOp",EDGE,"E26.0"),sQuery(id+"F13.wireOp",EDGE,"E27.0"),sQuery(id+"F13.wireOp",EDGE,"E28.0"),sQuery(id+"F13.wireOp",EDGE,"E29.0"),sQuery(id+"F13.wireOp",EDGE,"E30.0.0"),sQuery(id+"F13.wireOp",EDGE,"E30.0.1"),sQuery(id+"F13.wireOp",EDGE,"E30.0.2"),sQuery(id+"F13.wireOp",EDGE,"E30.0.3"),sQuery(id+"F13.wireOp",EDGE,"E30.0.4"),sQuery(id+"F13.wireOp",EDGE,"E30.0.5"),sQuery(id+"F13.wireOp",EDGE,"E30.0.6"),sQuery(id+"F13.wireOp",EDGE,"E30.0.7")])],"isStart":false});
            var sketch = newSketch(context, id + "F27", { "sketchPlane" : qUnion([Q0])});
            skCircle(sketch, "E77.0", {"center": v(-50, 50) * mm, "radius": 2 * mm, "construction": true});
            skCircle(sketch, "E78.0", {"center": v(-50, -50) * mm, "radius": 2 * mm, "construction": true});
            skCircle(sketch, "E79.0", {"center": v(50, -50) * mm, "radius": 2 * mm, "construction": true});
            skCircle(sketch, "E80.0", {"center": v(50, 50) * mm, "radius": 2 * mm, "construction": true});
            skCircle(sketch, "E81", {"center": v(-50, 50) * mm, "radius": 5 * mm});
            skCircle(sketch, "E82", {"center": v(50, 50) * mm, "radius": 5 * mm});
            skCircle(sketch, "E83", {"center": v(-50, -50) * mm, "radius": 5 * mm});
            skCircle(sketch, "E84", {"center": v(50, -50) * mm, "radius": 5 * mm});
            skSolve(sketch);
        }
        {
            var Q0;
            Q0 = qSketchRegion(id + "F27", true);
            var Q1;
            Q1=makeQuery(id+"F9.opExtrude","CAP_FACE",FACE,{"disambiguationData":[OSD([sQuery(id+"F8.wireOp",EDGE,"E16.0.0"),sQuery(id+"F8.wireOp",EDGE,"E16.0.1"),sQuery(id+"F8.wireOp",EDGE,"E16.0.2"),sQuery(id+"F8.wireOp",EDGE,"E16.0.3"),sQuery(id+"F8.wireOp",EDGE,"E16.0.4"),sQuery(id+"F8.wireOp",EDGE,"E16.0.5"),sQuery(id+"F8.wireOp",EDGE,"E16.0.6"),sQuery(id+"F8.wireOp",EDGE,"E16.0.7")])],"isStart":true});
            extrude(context, id + "F28", {"entities" : qUnion([Q0]), "operationType" : NewBodyOperationType.REMOVE, "endBound" : BoundingType.UP_TO_SURFACE, "oppositeDirection" : true, "depth" : 25 * mm, "endBoundEntityFace" : qUnion([Q1]), "offsetDistance" : 25 * mm});
        }
        {
            var Q0;
            Q0=makeQuery(id+"F1.opExtrude","SWEPT_BODY",BODY,{"disambiguationData":[OSD([sQuery(id+"F0.wireOp",EDGE,"E1"),sQuery(id+"F0.wireOp",EDGE,"E2"),sQuery(id+"F0.wireOp",EDGE,"E3"),sQuery(id+"F0.wireOp",EDGE,"E4"),sQuery(id+"F0.wireOp",EDGE,"E5.bottom"),sQuery(id+"F0.wireOp",EDGE,"E5.top"),sQuery(id+"F0.wireOp",EDGE,"E5.left"),sQuery(id+"F0.wireOp",EDGE,"E5.right")])]});
            transform(context, id + "F29", {"entities" : qUnion([Q0]), "transformType" : TransformType.TRANSLATION_3D, "dx" : 0 * mm, "dy" : 0 * mm, "dz" : -4 * mm, "makeCopy" : false});
        }
        {
            var Q0;
            Q0=makeQuery(id+"F4.opExtrude","CAP_FACE",FACE,{"disambiguationData":[OSD([sQuery(id+"F3.wireOp",EDGE,"E6.0.0"),sQuery(id+"F3.wireOp",EDGE,"E6.0.1"),sQuery(id+"F3.wireOp",EDGE,"E6.0.2"),sQuery(id+"F3.wireOp",EDGE,"E6.0.3"),sQuery(id+"F3.wireOp",EDGE,"E6.0.4"),sQuery(id+"F3.wireOp",EDGE,"E6.0.5"),sQuery(id+"F3.wireOp",EDGE,"E6.0.6"),sQuery(id+"F3.wireOp",EDGE,"E6.0.7"),sQuery(id+"F3.wireOp",EDGE,"E11"),sQuery(id+"F3.wireOp",EDGE,"E12"),sQuery(id+"F3.wireOp",EDGE,"E13"),sQuery(id+"F3.wireOp",EDGE,"E14")])],"isStart":true});
            var sketch = newSketch(context, id + "F30", { "sketchPlane" : qUnion([Q0])});
            skCircle(sketch, "E85.0", {"center": v(50, -50) * mm, "radius": 2 * mm});
            skCircle(sketch, "E86.0", {"center": v(-50, -50) * mm, "radius": 2 * mm});
            skCircle(sketch, "E87.0", {"center": v(-50, 50) * mm, "radius": 2 * mm});
            skCircle(sketch, "E88.0", {"center": v(50, 50) * mm, "radius": 2 * mm});
            skCircle(sketch, "E89.0", {"center": v(27.5, -27.5) * mm, "radius": 2 * mm});
            skLineSegment(sketch, "E90.0.0", {"start": v(50, 60) * mm, "end": v(-50, 60) * mm});
            skArc(sketch, "E90.0.1", {"start": v(-50, 60) * mm, "mid": v(-57.07, 57.07) * mm, "end": v(-60, 50) * mm});
            skLineSegment(sketch, "E90.0.2", {"start": v(-60, 50) * mm, "end": v(-60, -50) * mm});
            skArc(sketch, "E90.0.3", {"start": v(-60, -50) * mm, "mid": v(-57.07, -57.07) * mm, "end": v(-50, -60) * mm});
            skLineSegment(sketch, "E90.0.4", {"start": v(-50, -60) * mm, "end": v(50, -60) * mm});
            skArc(sketch, "E90.0.5", {"start": v(50, -60) * mm, "mid": v(57.07, -57.07) * mm, "end": v(60, -50) * mm});
            skLineSegment(sketch, "E90.0.6", {"start": v(60, -50) * mm, "end": v(60, 50) * mm});
            skArc(sketch, "E90.0.7", {"start": v(60, 50) * mm, "mid": v(57.07, 57.07) * mm, "end": v(50, 60) * mm});
            skCircle(sketch, "E91.0", {"center": v(-27.5, 27.5) * mm, "radius": 2 * mm});
            skCircle(sketch, "E92.0", {"center": v(27.5, 27.5) * mm, "radius": 2 * mm});
            skCircle(sketch, "E93.0", {"center": v(-27.5, -27.5) * mm, "radius": 2 * mm});
            skSolve(sketch);
        }
        {
            var Q0;
            Q0 = qSketchRegion(id + "F30", true);
            extrude(context, id + "F31", {"entities" : qUnion([Q0]), "depth" : 4 * mm, "offsetDistance" : 25 * mm});
        }
        {
            var Q0;
            Q0=makeQuery(id+"F1.opExtrude","CAP_FACE",FACE,{"disambiguationData":[OSD([sQuery(id+"F0.wireOp",EDGE,"E1"),sQuery(id+"F0.wireOp",EDGE,"E2"),sQuery(id+"F0.wireOp",EDGE,"E3"),sQuery(id+"F0.wireOp",EDGE,"E4"),sQuery(id+"F0.wireOp",EDGE,"E5.bottom"),sQuery(id+"F0.wireOp",EDGE,"E5.top"),sQuery(id+"F0.wireOp",EDGE,"E5.left"),sQuery(id+"F0.wireOp",EDGE,"E5.right")])],"isStart":true});
            var sketch = newSketch(context, id + "F32", { "sketchPlane" : qUnion([Q0])});
            skText(sketch, "E94", { "text": "1-1\n", "fontName": "OpenSans-Regular.ttf"});
            const initialGuessF32  = {"E94": [-0.015, -0.00826, 1, 0, 0.01652]};
            skSetInitialGuess(sketch, initialGuessF32);
            skSolve(sketch);
        }
        {
            var Q0;
            Q0 = qSketchRegion(id + "F32", true);
            extrude(context, id + "F33", {"entities" : qUnion([Q0]), "operationType" : NewBodyOperationType.REMOVE, "oppositeDirection" : true, "depth" : 1 * mm, "offsetDistance" : 25 * mm});
        }
        {
            var Q0;
            Q0=makeQuery(id+"F31.opExtrude","CAP_FACE",FACE,{"disambiguationData":[OSD([sQuery(id+"F30.wireOp",EDGE,"E85.0"),sQuery(id+"F30.wireOp",EDGE,"E86.0"),sQuery(id+"F30.wireOp",EDGE,"E87.0"),sQuery(id+"F30.wireOp",EDGE,"E88.0"),sQuery(id+"F30.wireOp",EDGE,"E89.0"),sQuery(id+"F30.wireOp",EDGE,"E91.0"),sQuery(id+"F30.wireOp",EDGE,"E92.0"),sQuery(id+"F30.wireOp",EDGE,"E90.0.6"),sQuery(id+"F30.wireOp",EDGE,"E90.0.7"),sQuery(id+"F30.wireOp",EDGE,"E90.0.0"),sQuery(id+"F30.wireOp",EDGE,"E90.0.1"),sQuery(id+"F30.wireOp",EDGE,"E90.0.2"),sQuery(id+"F30.wireOp",EDGE,"E90.0.3"),sQuery(id+"F30.wireOp",EDGE,"E90.0.4"),sQuery(id+"F30.wireOp",EDGE,"E90.0.5"),sQuery(id+"F30.wireOp",EDGE,"E93.0")])],"isStart":false});
            var sketch = newSketch(context, id + "F34", { "sketchPlane" : qUnion([Q0])});
            skText(sketch, "E95", { "text": "2-1", "fontName": "OpenSans-Regular.ttf"});
            const initialGuessF34  = {"E95": [-0.015, -0.00826, 1, 0, 0.01652]};
            skSetInitialGuess(sketch, initialGuessF34);
            skSolve(sketch);
        }
        {
            var Q0;
            Q0 = qSketchRegion(id + "F34", true);
            extrude(context, id + "F35", {"entities" : qUnion([Q0]), "operationType" : NewBodyOperationType.REMOVE, "oppositeDirection" : true, "depth" : 1 * mm, "offsetDistance" : 25 * mm});
        }
        {
            var Q0;
            Q0=makeQuery(id+"F4.opExtrude","CAP_FACE",FACE,{"disambiguationData":[OSD([sQuery(id+"F3.wireOp",EDGE,"E6.0.0"),sQuery(id+"F3.wireOp",EDGE,"E6.0.1"),sQuery(id+"F3.wireOp",EDGE,"E6.0.2"),sQuery(id+"F3.wireOp",EDGE,"E6.0.3"),sQuery(id+"F3.wireOp",EDGE,"E6.0.4"),sQuery(id+"F3.wireOp",EDGE,"E6.0.5"),sQuery(id+"F3.wireOp",EDGE,"E6.0.6"),sQuery(id+"F3.wireOp",EDGE,"E6.0.7"),sQuery(id+"F3.wireOp",EDGE,"E11"),sQuery(id+"F3.wireOp",EDGE,"E12"),sQuery(id+"F3.wireOp",EDGE,"E13"),sQuery(id+"F3.wireOp",EDGE,"E14")])],"isStart":true});
            var sketch = newSketch(context, id + "F36", { "sketchPlane" : qUnion([Q0])});
            skText(sketch, "E96", { "text": "3-1", "fontName": "OpenSans-Regular.ttf"});
            const initialGuessF36  = {"E96": [-0.015, -0.00826, 1, 0, 0.01652]};
            skSetInitialGuess(sketch, initialGuessF36);
            skSolve(sketch);
        }
        {
            var Q0;
            Q0 = qSketchRegion(id + "F36", true);
            extrude(context, id + "F37", {"entities" : qUnion([Q0]), "operationType" : NewBodyOperationType.REMOVE, "oppositeDirection" : true, "depth" : 1 * mm, "offsetDistance" : 25 * mm});
        }
        {
            var Q0;
            Q0=makeQuery(id+"F6.opExtrude","CAP_FACE",FACE,{"disambiguationData":[OSD([sQuery(id+"F5.wireOp",EDGE,"E15.bottom"),sQuery(id+"F5.wireOp",EDGE,"E15.top"),sQuery(id+"F5.wireOp",EDGE,"E15.left"),sQuery(id+"F5.wireOp",EDGE,"E15.right")])],"isStart":true});
            var sketch = newSketch(context, id + "F38", { "sketchPlane" : qUnion([Q0])});
            skText(sketch, "E97", { "text": "4-1", "fontName": "OpenSans-Regular.ttf"});
            const initialGuessF38  = {"E97": [-0.015, -0.00826, 1, 0, 0.01652]};
            skSetInitialGuess(sketch, initialGuessF38);
            skSolve(sketch);
        }
        {
            var Q0;
            Q0 = qSketchRegion(id + "F38", true);
            extrude(context, id + "F39", {"entities" : qUnion([Q0]), "operationType" : NewBodyOperationType.REMOVE, "oppositeDirection" : true, "depth" : 1 * mm, "offsetDistance" : 25 * mm});
        }
        {
            var Q0;
            Q0=makeQuery(id+"F9.opExtrude","CAP_FACE",FACE,{"disambiguationData":[OSD([sQuery(id+"F8.wireOp",EDGE,"E16.0.0"),sQuery(id+"F8.wireOp",EDGE,"E16.0.1"),sQuery(id+"F8.wireOp",EDGE,"E16.0.2"),sQuery(id+"F8.wireOp",EDGE,"E16.0.3"),sQuery(id+"F8.wireOp",EDGE,"E16.0.4"),sQuery(id+"F8.wireOp",EDGE,"E16.0.5"),sQuery(id+"F8.wireOp",EDGE,"E16.0.6"),sQuery(id+"F8.wireOp",EDGE,"E16.0.7")])],"isStart":true});
            var sketch = newSketch(context, id + "F40", { "sketchPlane" : qUnion([Q0])});
            skText(sketch, "E98", { "text": "5-1", "fontName": "OpenSans-Regular.ttf"});
            const initialGuessF40  = {"E98": [-0.015, -0.00826, 1, 0, 0.01652]};
            skSetInitialGuess(sketch, initialGuessF40);
            skSolve(sketch);
        }
        {
            var Q0;
            Q0 = qSketchRegion(id + "F40", true);
            extrude(context, id + "F41", {"entities" : qUnion([Q0]), "operationType" : NewBodyOperationType.REMOVE, "oppositeDirection" : true, "depth" : 1 * mm, "offsetDistance" : 25 * mm});
        }
        {
            var Q0;
            Q0=makeQuery(id+"F14.opExtrude","CAP_FACE",FACE,{"disambiguationData":[OSD([sQuery(id+"F13.wireOp",EDGE,"E26.0"),sQuery(id+"F13.wireOp",EDGE,"E27.0"),sQuery(id+"F13.wireOp",EDGE,"E28.0"),sQuery(id+"F13.wireOp",EDGE,"E29.0"),sQuery(id+"F13.wireOp",EDGE,"E30.0.0"),sQuery(id+"F13.wireOp",EDGE,"E30.0.1"),sQuery(id+"F13.wireOp",EDGE,"E30.0.2"),sQuery(id+"F13.wireOp",EDGE,"E30.0.3"),sQuery(id+"F13.wireOp",EDGE,"E30.0.4"),sQuery(id+"F13.wireOp",EDGE,"E30.0.5"),sQuery(id+"F13.wireOp",EDGE,"E30.0.6"),sQuery(id+"F13.wireOp",EDGE,"E30.0.7")])],"isStart":true});
            var sketch = newSketch(context, id + "F42", { "sketchPlane" : qUnion([Q0])});
            skText(sketch, "E99", { "text": "6-1", "fontName": "OpenSans-Regular.ttf"});
            const initialGuessF42  = {"E99": [-0.015, -0.00826, 1, 0, 0.01652]};
            skSetInitialGuess(sketch, initialGuessF42);
            skSolve(sketch);
        }
        {
            var Q0;
            Q0 = qSketchRegion(id + "F42", true);
            extrude(context, id + "F43", {"entities" : qUnion([Q0]), "operationType" : NewBodyOperationType.ADD, "depth" : 1 * mm, "offsetDistance" : 25 * mm});
        }
        {
            var Q0;
            Q0=makeQuery(id+"F24.opExtrude","CAP_FACE",FACE,{"disambiguationData":[OSD([sQuery(id+"F23.wireOp",EDGE,"E60.0.3"),sQuery(id+"F23.wireOp",EDGE,"E60.0.4"),sQuery(id+"F23.wireOp",EDGE,"E60.0.5"),sQuery(id+"F23.wireOp",EDGE,"E60.0.6"),sQuery(id+"F23.wireOp",EDGE,"E60.0.7"),sQuery(id+"F23.wireOp",EDGE,"E60.0.8"),sQuery(id+"F23.wireOp",EDGE,"E60.0.9"),sQuery(id+"F23.wireOp",EDGE,"E60.0.10"),sQuery(id+"F23.wireOp",EDGE,"E60.0.11"),sQuery(id+"F23.wireOp",EDGE,"E61.0.0"),sQuery(id+"F23.wireOp",EDGE,"E61.0.1"),sQuery(id+"F23.wireOp",EDGE,"E61.0.2"),sQuery(id+"F23.wireOp",EDGE,"E61.0.3"),sQuery(id+"F23.wireOp",EDGE,"E61.0.4"),sQuery(id+"F23.wireOp",EDGE,"E62"),sQuery(id+"F23.wireOp",EDGE,"E63"),sQuery(id+"F23.wireOp",EDGE,"E64"),sQuery(id+"F23.wireOp",EDGE,"E65"),sQuery(id+"F23.wireOp",EDGE,"E66.filletArc"),sQuery(id+"F23.wireOp",EDGE,"E67.filletArc")])],"isStart":false});
            var sketch = newSketch(context, id + "F44", { "sketchPlane" : qUnion([Q0])});
            skLineSegment(sketch, "E100", {"start": v(0, 82.5) * mm, "end": v(0, 37.5) * mm, "construction": true});
            skPoint(sketch, "E101", {"position": v(0, 60) * mm});
            skText(sketch, "E102", { "text": "1-2", "fontName": "OpenSans-Regular.ttf"});
            const initialGuessF44  = {"E102": [-0.015, 0.04518, 1, 0, 0.01463]};
            skSetInitialGuess(sketch, initialGuessF44);
            skSolve(sketch);
        }
        {
            var Q0;
            Q0 = qSketchRegion(id + "F44", true);
            extrude(context, id + "F45", {"entities" : qUnion([Q0]), "operationType" : NewBodyOperationType.REMOVE, "oppositeDirection" : true, "depth" : 1 * mm, "offsetDistance" : 25 * mm});
        }
        {
            var Q0;
            Q0=makeQuery(id+"F22.opExtrude","CAP_FACE",FACE,{"disambiguationData":[OSD([sQuery(id+"F21.wireOp",EDGE,"E59.0.0"),sQuery(id+"F21.wireOp",EDGE,"E59.0.1"),sQuery(id+"F21.wireOp",EDGE,"E59.0.2"),sQuery(id+"F21.wireOp",EDGE,"E59.0.3"),sQuery(id+"F21.wireOp",EDGE,"E59.0.4"),sQuery(id+"F21.wireOp",EDGE,"E59.0.5"),sQuery(id+"F21.wireOp",EDGE,"E59.0.6"),sQuery(id+"F21.wireOp",EDGE,"E59.0.7"),sQuery(id+"F21.wireOp",EDGE,"E59.0.8"),sQuery(id+"F21.wireOp",EDGE,"E59.0.9"),sQuery(id+"F21.wireOp",EDGE,"E59.0.10"),sQuery(id+"F21.wireOp",EDGE,"E59.0.11"),sQuery(id+"F21.wireOp",EDGE,"E59.0.12"),sQuery(id+"F21.wireOp",EDGE,"E59.0.13"),sQuery(id+"F21.wireOp",EDGE,"E59.0.14"),sQuery(id+"F21.wireOp",EDGE,"E59.0.15")])],"isStart":false});
            var sketch = newSketch(context, id + "F46", { "sketchPlane" : qUnion([Q0])});
            skLineSegment(sketch, "E103", {"start": v(0, 60) * mm, "end": v(0, 82.5) * mm, "construction": true});
            skPoint(sketch, "E104", {"position": v(0, 71.25) * mm});
            skText(sketch, "E105", { "text": "2-2", "fontName": "OpenSans-Regular.ttf"});
            const initialGuessF46  = {"E105": [-0.015, 0.05393, 1, 0, 0.01463]};
            skSetInitialGuess(sketch, initialGuessF46);
            skSolve(sketch);
        }
        {
            var Q0;
            Q0 = qSketchRegion(id + "F46", true);
            extrude(context, id + "F47", {"entities" : qUnion([Q0]), "operationType" : NewBodyOperationType.REMOVE, "oppositeDirection" : true, "depth" : 1 * mm, "offsetDistance" : 25 * mm});
        }
        {
            var Q0;
            Q0=makeQuery(id+"F19.opExtrude","CAP_FACE",FACE,{"disambiguationData":[OSD([sQuery(id+"F18.wireOp",EDGE,"E43.0"),sQuery(id+"F18.wireOp",EDGE,"E44.0"),sQuery(id+"F18.wireOp",EDGE,"E45.0"),sQuery(id+"F18.wireOp",EDGE,"E46.0"),sQuery(id+"F18.wireOp",EDGE,"E47.0"),sQuery(id+"F18.wireOp",EDGE,"E48.0"),sQuery(id+"F18.wireOp",EDGE,"E49.0"),sQuery(id+"F18.wireOp",EDGE,"E50.0"),sQuery(id+"F18.wireOp",EDGE,"E51.0"),sQuery(id+"F18.wireOp",EDGE,"E52.0"),sQuery(id+"F18.wireOp",EDGE,"E53.0"),sQuery(id+"F18.wireOp",EDGE,"E54.0"),sQuery(id+"F18.wireOp",EDGE,"E55"),sQuery(id+"F18.wireOp",EDGE,"E56"),sQuery(id+"F18.wireOp",EDGE,"E57"),sQuery(id+"F18.wireOp",EDGE,"E58")])],"isStart":false});
            var sketch = newSketch(context, id + "F48", { "sketchPlane" : qUnion([Q0])});
            skLineSegment(sketch, "E106", {"start": v(0, 60) * mm, "end": v(0, 82.5) * mm, "construction": true});
            skPoint(sketch, "E107", {"position": v(0, 71.25) * mm});
            skText(sketch, "E108", { "text": "3-2", "fontName": "OpenSans-Regular.ttf"});
            const initialGuessF48  = {"E108": [-0.015, 0.05393, 1, 0, 0.01463]};
            skSetInitialGuess(sketch, initialGuessF48);
            skSolve(sketch);
        }
        {
            var Q0;
            Q0 = qSketchRegion(id + "F48", true);
            extrude(context, id + "F49", {"entities" : qUnion([Q0]), "operationType" : NewBodyOperationType.REMOVE, "oppositeDirection" : true, "depth" : 1 * mm, "offsetDistance" : 25 * mm});
        }
        {
            var Q0;
            Q0=makeQuery(id+"F16.opExtrude","CAP_FACE",FACE,{"disambiguationData":[OSD([sQuery(id+"F15.wireOp",EDGE,"E31"),sQuery(id+"F15.wireOp",EDGE,"E32"),sQuery(id+"F15.wireOp",EDGE,"E33"),sQuery(id+"F15.wireOp",EDGE,"E34"),sQuery(id+"F15.wireOp",EDGE,"E35"),sQuery(id+"F15.wireOp",EDGE,"E38.MirrorCS"),sQuery(id+"F15.wireOp",EDGE,"E39.MirrorCS"),sQuery(id+"F15.wireOp",EDGE,"E40.MirrorCS"),sQuery(id+"F15.wireOp",EDGE,"E41.MirrorCS"),sQuery(id+"F15.wireOp",EDGE,"E42.MirrorCS")])],"isStart":true});
            var sketch = newSketch(context, id + "F50", { "sketchPlane" : qUnion([Q0])});
            skLineSegment(sketch, "E109", {"start": v(0, 32.5) * mm, "end": v(0, 82.5) * mm, "construction": true});
            skPoint(sketch, "E110", {"position": v(0, 57.5) * mm});
            skText(sketch, "E111", { "text": "4-2", "fontName": "OpenSans-Regular.ttf"});
            const initialGuessF50  = {"E111": [-0.015, 0.04268, 1, 0, 0.01463]};
            skSetInitialGuess(sketch, initialGuessF50);
            skSolve(sketch);
        }
        {
            var Q0;
            Q0 = qSketchRegion(id + "F50", true);
            extrude(context, id + "F51", {"entities" : qUnion([Q0]), "operationType" : NewBodyOperationType.REMOVE, "oppositeDirection" : true, "depth" : 1 * mm, "offsetDistance" : 25 * mm});
        }
    });
